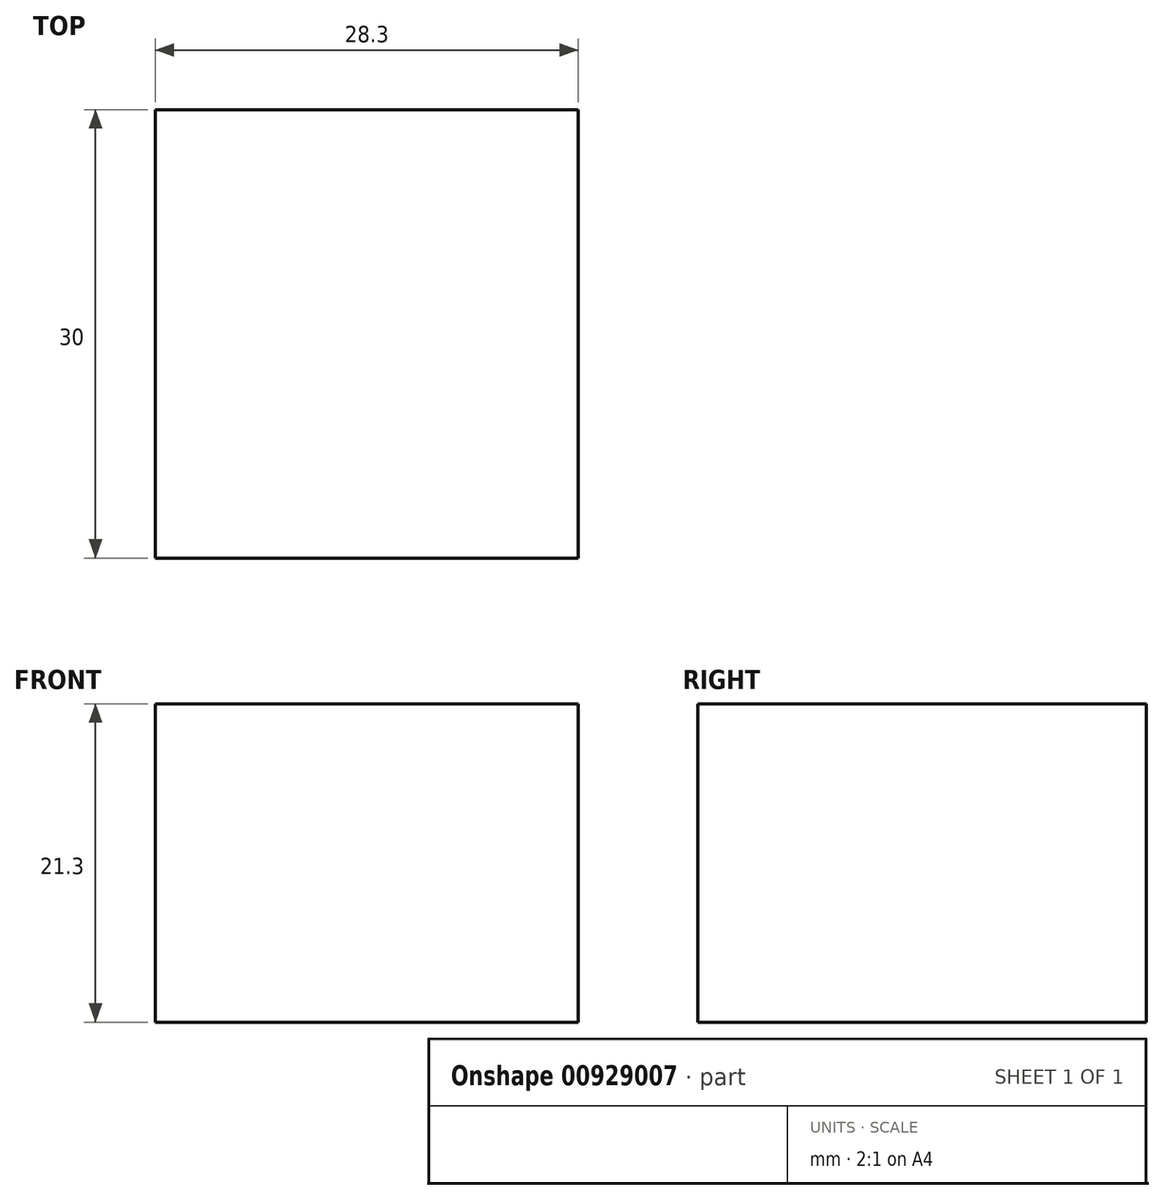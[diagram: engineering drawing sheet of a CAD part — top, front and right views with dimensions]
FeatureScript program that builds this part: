
annotation { "Feature Type Name" : "Feature", "Feature Type Description" : "" }
export const myFeature = defineFeature(function(context is Context, id is Id, definition is map)
    precondition{}
    {
        {
            var Q0;
            Q0=qCreatedBy(makeId("Front.planeOp"),FACE);
            var sketch = newSketch(context, id + "F0", { "sketchPlane" : qUnion([Q0])});
            skLineSegment(sketch, "E0.bottom", {"start": v(15.3, 12.75) * mm, "end": v(-15.3, 12.75) * mm});
            skLineSegment(sketch, "E0.top", {"start": v(15.3, -12.75) * mm, "end": v(-15.3, -12.75) * mm});
            skLineSegment(sketch, "E0.left", {"start": v(15.3, 12.75) * mm, "end": v(15.3, -12.75) * mm});
            skLineSegment(sketch, "E0.right", {"start": v(-15.3, 12.75) * mm, "end": v(-15.3, -12.75) * mm});
            skPoint(sketch, "E0.middle", {"position": v(0, 0) * mm});
            skLineSegment(sketch, "E1.bottom", {"start": v(14.15, 10.65) * mm, "end": v(-14.15, 10.65) * mm});
            skLineSegment(sketch, "E1.top", {"start": v(14.15, -10.65) * mm, "end": v(-14.15, -10.65) * mm});
            skLineSegment(sketch, "E1.left", {"start": v(14.15, 10.65) * mm, "end": v(14.15, -10.65) * mm});
            skLineSegment(sketch, "E1.right", {"start": v(-14.15, 10.65) * mm, "end": v(-14.15, -10.65) * mm});
            skSolve(sketch);
        }
        {
            var Q0;
            Q0=makeQuery(id+"F0.imprint","IMPRINT",FACE,{"disambiguationData":[TD([[makeQuery(id+"F0.imprint","IMPRINT",EDGE,{"derivedFrom":sQuery(id+"F0.wireOp",EDGE,"E1.bottom")}),1.0]])]});
            extrude(context, id + "F1", {"entities" : qUnion([Q0]), "oppositeDirection" : true, "depth" : 30 * mm, "offsetDistance" : 25 * mm});
        }
    });
